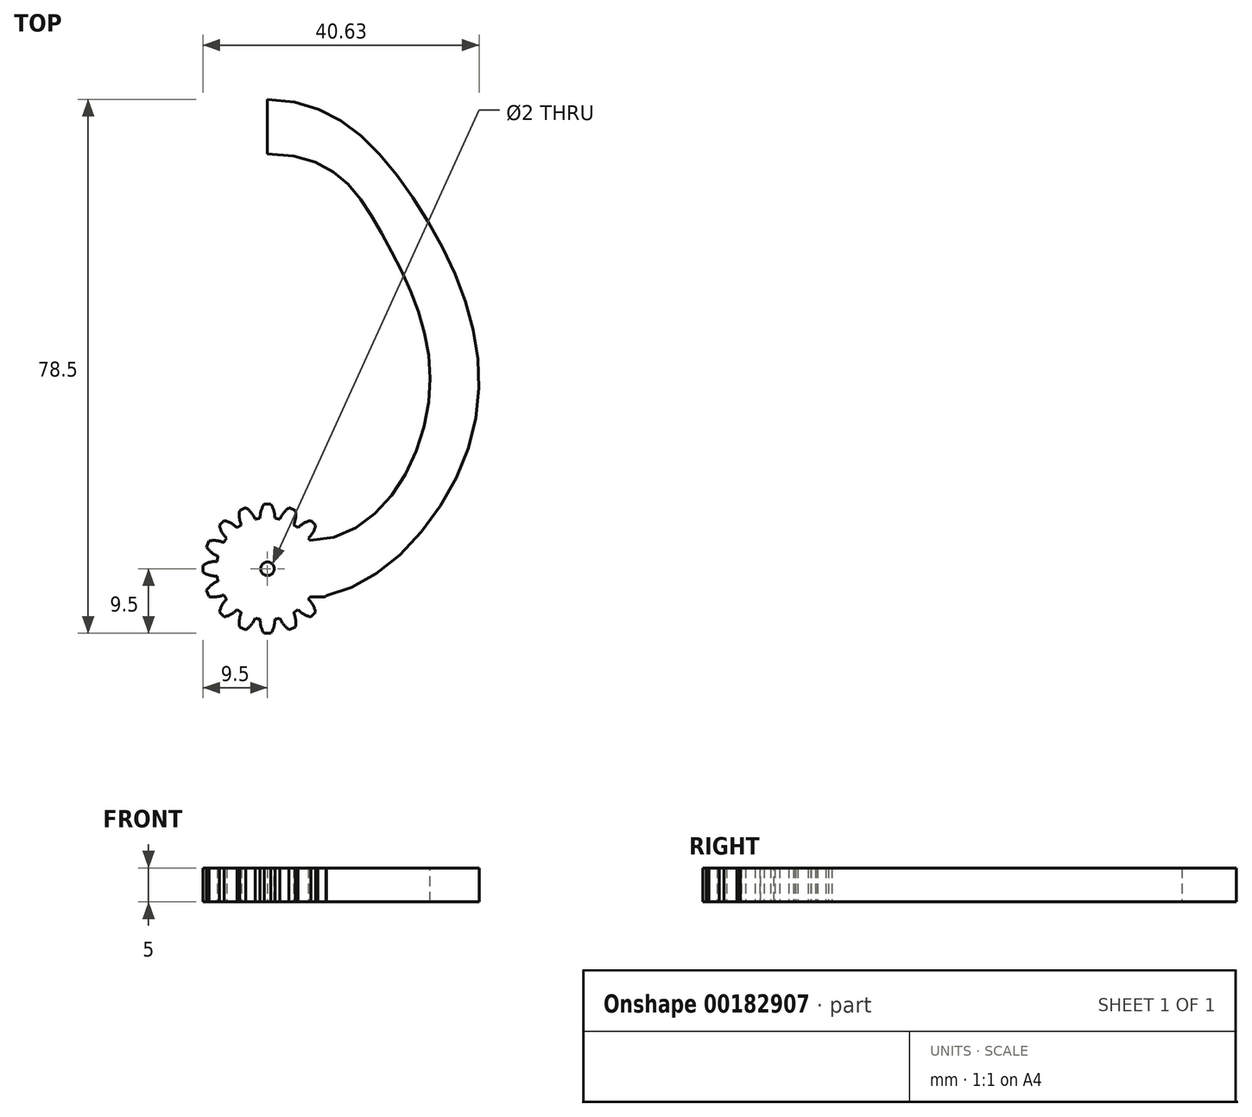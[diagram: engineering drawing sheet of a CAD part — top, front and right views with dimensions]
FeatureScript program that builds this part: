
annotation { "Feature Type Name" : "Feature", "Feature Type Description" : "" }
export const myFeature = defineFeature(function(context is Context, id is Id, definition is map)
    precondition{}
    {
        {
            var Q0;
            Q0=qCreatedBy(makeId("Top.planeOp"),FACE);
            var sketch = newSketch(context, id + "F0", { "sketchPlane" : qUnion([Q0])});
            skCircle(sketch, "E0", {"center": v(0, 0) * mm, "radius": 7.5 * mm});
            skLineSegment(sketch, "E1", {"start": v(0, 0) * mm, "end": v(0, 7.5) * mm, "construction": true});
            skLineSegment(sketch, "E2", {"start": v(0, 7.5) * mm, "end": v(0, 9.5) * mm, "construction": true});
            skLineSegment(sketch, "E3", {"start": v(0, 9.5) * mm, "end": v(-0.5, 9.5) * mm});
            skArc(sketch, "E4", {"start": v(-0.5, 9.5) * mm, "mid": v(-0.95, 8.5) * mm, "end": v(-1.09, 7.42) * mm});
            skLineSegment(sketch, "E5.MirrorCS", {"start": v(0, 9.5) * mm, "end": v(0.5, 9.5) * mm});
            skArc(sketch, "E6.MirrorCS", {"start": v(0.5, 9.5) * mm, "mid": v(0.95, 8.5) * mm, "end": v(1.09, 7.42) * mm});
            skArc(sketch, "E7.1.0", {"start": v(-4.1, 8.59) * mm, "mid": v(-4.13, 7.5) * mm, "end": v(-3.85, 6.44) * mm});
            skLineSegment(sketch, "E7.1.1", {"start": v(-3.64, 8.78) * mm, "end": v(-4.1, 8.59) * mm});
            skLineSegment(sketch, "E7.1.2", {"start": v(-3.64, 8.78) * mm, "end": v(-3.17, 8.97) * mm});
            skArc(sketch, "E7.1.3", {"start": v(-3.17, 8.97) * mm, "mid": v(-2.38, 8.22) * mm, "end": v(-1.83, 7.27) * mm});
            skArc(sketch, "E7.2.0", {"start": v(-7.07, 6.36) * mm, "mid": v(-6.69, 5.34) * mm, "end": v(-6.02, 4.48) * mm});
            skLineSegment(sketch, "E7.2.1", {"start": v(-6.72, 6.72) * mm, "end": v(-7.07, 6.36) * mm});
            skLineSegment(sketch, "E7.2.2", {"start": v(-6.72, 6.72) * mm, "end": v(-6.36, 7.07) * mm});
            skArc(sketch, "E7.2.3", {"start": v(-6.36, 7.07) * mm, "mid": v(-5.34, 6.69) * mm, "end": v(-4.48, 6.02) * mm});
            skArc(sketch, "E7.3.0", {"start": v(-8.97, 3.17) * mm, "mid": v(-8.22, 2.38) * mm, "end": v(-7.27, 1.83) * mm});
            skLineSegment(sketch, "E7.3.1", {"start": v(-8.78, 3.64) * mm, "end": v(-8.97, 3.17) * mm});
            skLineSegment(sketch, "E7.3.2", {"start": v(-8.78, 3.64) * mm, "end": v(-8.59, 4.1) * mm});
            skArc(sketch, "E7.3.3", {"start": v(-8.59, 4.1) * mm, "mid": v(-7.5, 4.13) * mm, "end": v(-6.44, 3.85) * mm});
            skArc(sketch, "E7.4.0", {"start": v(-9.5, -0.5) * mm, "mid": v(-8.5, -0.95) * mm, "end": v(-7.42, -1.09) * mm});
            skLineSegment(sketch, "E7.4.1", {"start": v(-9.5, 0) * mm, "end": v(-9.5, -0.5) * mm});
            skLineSegment(sketch, "E7.4.2", {"start": v(-9.5, 0) * mm, "end": v(-9.5, 0.5) * mm});
            skArc(sketch, "E7.4.3", {"start": v(-9.5, 0.5) * mm, "mid": v(-8.5, 0.95) * mm, "end": v(-7.42, 1.09) * mm});
            skArc(sketch, "E7.5.0", {"start": v(-8.59, -4.1) * mm, "mid": v(-7.5, -4.13) * mm, "end": v(-6.44, -3.85) * mm});
            skLineSegment(sketch, "E7.5.1", {"start": v(-8.78, -3.64) * mm, "end": v(-8.59, -4.1) * mm});
            skLineSegment(sketch, "E7.5.2", {"start": v(-8.78, -3.64) * mm, "end": v(-8.97, -3.17) * mm});
            skArc(sketch, "E7.5.3", {"start": v(-8.97, -3.17) * mm, "mid": v(-8.22, -2.38) * mm, "end": v(-7.27, -1.83) * mm});
            skArc(sketch, "E7.6.0", {"start": v(-6.36, -7.07) * mm, "mid": v(-5.34, -6.69) * mm, "end": v(-4.48, -6.02) * mm});
            skLineSegment(sketch, "E7.6.1", {"start": v(-6.72, -6.72) * mm, "end": v(-6.36, -7.07) * mm});
            skLineSegment(sketch, "E7.6.2", {"start": v(-6.72, -6.72) * mm, "end": v(-7.07, -6.36) * mm});
            skArc(sketch, "E7.6.3", {"start": v(-7.07, -6.36) * mm, "mid": v(-6.69, -5.34) * mm, "end": v(-6.02, -4.48) * mm});
            skArc(sketch, "E7.7.0", {"start": v(-3.17, -8.97) * mm, "mid": v(-2.38, -8.22) * mm, "end": v(-1.83, -7.27) * mm});
            skLineSegment(sketch, "E7.7.1", {"start": v(-3.64, -8.78) * mm, "end": v(-3.17, -8.97) * mm});
            skLineSegment(sketch, "E7.7.2", {"start": v(-3.64, -8.78) * mm, "end": v(-4.1, -8.59) * mm});
            skArc(sketch, "E7.7.3", {"start": v(-4.1, -8.59) * mm, "mid": v(-4.13, -7.5) * mm, "end": v(-3.85, -6.44) * mm});
            skArc(sketch, "E7.8.0", {"start": v(0.5, -9.5) * mm, "mid": v(0.95, -8.5) * mm, "end": v(1.09, -7.42) * mm});
            skLineSegment(sketch, "E7.8.1", {"start": v(0, -9.5) * mm, "end": v(0.5, -9.5) * mm});
            skLineSegment(sketch, "E7.8.2", {"start": v(0, -9.5) * mm, "end": v(-0.5, -9.5) * mm});
            skArc(sketch, "E7.8.3", {"start": v(-0.5, -9.5) * mm, "mid": v(-0.95, -8.5) * mm, "end": v(-1.09, -7.42) * mm});
            skArc(sketch, "E7.9.0", {"start": v(4.1, -8.59) * mm, "mid": v(4.13, -7.5) * mm, "end": v(3.85, -6.44) * mm});
            skLineSegment(sketch, "E7.9.1", {"start": v(3.64, -8.78) * mm, "end": v(4.1, -8.59) * mm});
            skLineSegment(sketch, "E7.9.2", {"start": v(3.64, -8.78) * mm, "end": v(3.17, -8.97) * mm});
            skArc(sketch, "E7.9.3", {"start": v(3.17, -8.97) * mm, "mid": v(2.38, -8.22) * mm, "end": v(1.83, -7.27) * mm});
            skArc(sketch, "E7.10.0", {"start": v(7.07, -6.36) * mm, "mid": v(6.69, -5.34) * mm, "end": v(6.02, -4.48) * mm});
            skLineSegment(sketch, "E7.10.1", {"start": v(6.72, -6.72) * mm, "end": v(7.07, -6.36) * mm});
            skLineSegment(sketch, "E7.10.2", {"start": v(6.72, -6.72) * mm, "end": v(6.36, -7.07) * mm});
            skArc(sketch, "E7.10.3", {"start": v(6.36, -7.07) * mm, "mid": v(5.34, -6.69) * mm, "end": v(4.48, -6.02) * mm});
            skArc(sketch, "E7.11.0", {"start": v(8.97, -3.17) * mm, "mid": v(8.22, -2.38) * mm, "end": v(7.27, -1.83) * mm});
            skLineSegment(sketch, "E7.11.1", {"start": v(8.78, -3.64) * mm, "end": v(8.97, -3.17) * mm});
            skLineSegment(sketch, "E7.11.2", {"start": v(8.78, -3.64) * mm, "end": v(8.59, -4.1) * mm});
            skArc(sketch, "E7.11.3", {"start": v(8.59, -4.1) * mm, "mid": v(7.5, -4.13) * mm, "end": v(6.44, -3.85) * mm});
            skArc(sketch, "E7.12.0", {"start": v(9.5, 0.5) * mm, "mid": v(8.5, 0.95) * mm, "end": v(7.42, 1.09) * mm});
            skLineSegment(sketch, "E7.12.1", {"start": v(9.5, 0) * mm, "end": v(9.5, 0.5) * mm});
            skLineSegment(sketch, "E7.12.2", {"start": v(9.5, 0) * mm, "end": v(9.5, -0.5) * mm});
            skArc(sketch, "E7.12.3", {"start": v(9.5, -0.5) * mm, "mid": v(8.5, -0.95) * mm, "end": v(7.42, -1.09) * mm});
            skArc(sketch, "E7.13.0", {"start": v(8.59, 4.1) * mm, "mid": v(7.5, 4.13) * mm, "end": v(6.44, 3.85) * mm});
            skLineSegment(sketch, "E7.13.1", {"start": v(8.78, 3.64) * mm, "end": v(8.59, 4.1) * mm});
            skLineSegment(sketch, "E7.13.2", {"start": v(8.78, 3.64) * mm, "end": v(8.97, 3.17) * mm});
            skArc(sketch, "E7.13.3", {"start": v(8.97, 3.17) * mm, "mid": v(8.22, 2.38) * mm, "end": v(7.27, 1.83) * mm});
            skArc(sketch, "E7.14.0", {"start": v(6.36, 7.07) * mm, "mid": v(5.34, 6.69) * mm, "end": v(4.48, 6.02) * mm});
            skLineSegment(sketch, "E7.14.1", {"start": v(6.72, 6.72) * mm, "end": v(6.36, 7.07) * mm});
            skLineSegment(sketch, "E7.14.2", {"start": v(6.72, 6.72) * mm, "end": v(7.07, 6.36) * mm});
            skArc(sketch, "E7.14.3", {"start": v(7.07, 6.36) * mm, "mid": v(6.69, 5.34) * mm, "end": v(6.02, 4.48) * mm});
            skArc(sketch, "E7.15.0", {"start": v(3.17, 8.97) * mm, "mid": v(2.38, 8.22) * mm, "end": v(1.83, 7.27) * mm});
            skLineSegment(sketch, "E7.15.1", {"start": v(3.64, 8.78) * mm, "end": v(3.17, 8.97) * mm});
            skLineSegment(sketch, "E7.15.2", {"start": v(3.64, 8.78) * mm, "end": v(4.1, 8.59) * mm});
            skArc(sketch, "E7.15.3", {"start": v(4.1, 8.59) * mm, "mid": v(4.13, 7.5) * mm, "end": v(3.85, 6.44) * mm});
            skSolve(sketch);
        }
        {
            var Q0;
            Q0=qSketchRegion(id+"F0",true);
            extrude(context, id + "F1", {"entities" : qUnion([Q0]), "depth" : 5 * mm});
        }
        {
            var Q0;
            Q0=makeQuery(id+"F1.opExtrude","CAP_FACE",FACE,{"disambiguationData":[OSD([sQuery(id+"F0.wireOp",EDGE,"E0"),sQuery(id+"F0.wireOp",EDGE,"E3"),sQuery(id+"F0.wireOp",EDGE,"E4"),sQuery(id+"F0.wireOp",EDGE,"E5.MirrorCS"),sQuery(id+"F0.wireOp",EDGE,"E6.MirrorCS"),sQuery(id+"F0.wireOp",EDGE,"E7.1.0"),sQuery(id+"F0.wireOp",EDGE,"E7.1.1"),sQuery(id+"F0.wireOp",EDGE,"E7.1.2"),sQuery(id+"F0.wireOp",EDGE,"E7.1.3"),sQuery(id+"F0.wireOp",EDGE,"E7.2.0"),sQuery(id+"F0.wireOp",EDGE,"E7.2.1"),sQuery(id+"F0.wireOp",EDGE,"E7.2.2"),sQuery(id+"F0.wireOp",EDGE,"E7.2.3"),sQuery(id+"F0.wireOp",EDGE,"E7.3.0"),sQuery(id+"F0.wireOp",EDGE,"E7.3.1"),sQuery(id+"F0.wireOp",EDGE,"E7.3.2"),sQuery(id+"F0.wireOp",EDGE,"E7.3.3"),sQuery(id+"F0.wireOp",EDGE,"E7.4.0"),sQuery(id+"F0.wireOp",EDGE,"E7.4.1"),sQuery(id+"F0.wireOp",EDGE,"E7.4.2"),sQuery(id+"F0.wireOp",EDGE,"E7.4.3"),sQuery(id+"F0.wireOp",EDGE,"E7.5.0"),sQuery(id+"F0.wireOp",EDGE,"E7.5.1"),sQuery(id+"F0.wireOp",EDGE,"E7.5.2"),sQuery(id+"F0.wireOp",EDGE,"E7.5.3"),sQuery(id+"F0.wireOp",EDGE,"E7.6.0"),sQuery(id+"F0.wireOp",EDGE,"E7.6.1"),sQuery(id+"F0.wireOp",EDGE,"E7.6.2"),sQuery(id+"F0.wireOp",EDGE,"E7.6.3"),sQuery(id+"F0.wireOp",EDGE,"E7.7.0"),sQuery(id+"F0.wireOp",EDGE,"E7.7.1"),sQuery(id+"F0.wireOp",EDGE,"E7.7.2"),sQuery(id+"F0.wireOp",EDGE,"E7.7.3"),sQuery(id+"F0.wireOp",EDGE,"E7.8.0"),sQuery(id+"F0.wireOp",EDGE,"E7.8.1"),sQuery(id+"F0.wireOp",EDGE,"E7.8.2"),sQuery(id+"F0.wireOp",EDGE,"E7.8.3"),sQuery(id+"F0.wireOp",EDGE,"E7.9.0"),sQuery(id+"F0.wireOp",EDGE,"E7.9.1"),sQuery(id+"F0.wireOp",EDGE,"E7.9.2"),sQuery(id+"F0.wireOp",EDGE,"E7.9.3"),sQuery(id+"F0.wireOp",EDGE,"E7.10.0"),sQuery(id+"F0.wireOp",EDGE,"E7.10.1"),sQuery(id+"F0.wireOp",EDGE,"E7.10.2"),sQuery(id+"F0.wireOp",EDGE,"E7.10.3"),sQuery(id+"F0.wireOp",EDGE,"E7.11.0"),sQuery(id+"F0.wireOp",EDGE,"E7.11.1"),sQuery(id+"F0.wireOp",EDGE,"E7.11.2"),sQuery(id+"F0.wireOp",EDGE,"E7.11.3"),sQuery(id+"F0.wireOp",EDGE,"E7.12.0"),sQuery(id+"F0.wireOp",EDGE,"E7.12.1"),sQuery(id+"F0.wireOp",EDGE,"E7.12.2"),sQuery(id+"F0.wireOp",EDGE,"E7.12.3"),sQuery(id+"F0.wireOp",EDGE,"E7.13.0"),sQuery(id+"F0.wireOp",EDGE,"E7.13.1"),sQuery(id+"F0.wireOp",EDGE,"E7.13.2"),sQuery(id+"F0.wireOp",EDGE,"E7.13.3"),sQuery(id+"F0.wireOp",EDGE,"E7.14.0"),sQuery(id+"F0.wireOp",EDGE,"E7.14.1"),sQuery(id+"F0.wireOp",EDGE,"E7.14.2"),sQuery(id+"F0.wireOp",EDGE,"E7.14.3"),sQuery(id+"F0.wireOp",EDGE,"E7.15.0"),sQuery(id+"F0.wireOp",EDGE,"E7.15.1"),sQuery(id+"F0.wireOp",EDGE,"E7.15.2"),sQuery(id+"F0.wireOp",EDGE,"E7.15.3")])],"isStart":false});
            var sketch = newSketch(context, id + "F2", { "sketchPlane" : qUnion([Q0])});
            skCircle(sketch, "E8", {"center": v(0, 0) * mm, "radius": 1 * mm});
            skSolve(sketch);
        }
        {
            var Q0;
            Q0=qSketchRegion(id+"F2",true);
            extrude(context, id + "F3", {"entities" : qUnion([Q0]), "operationType" : NewBodyOperationType.REMOVE, "endBound" : BoundingType.THROUGH_ALL, "oppositeDirection" : true, "depth" : 25 * mm});
        }
        {
            var Q0;
            Q0=qCreatedBy(makeId("Top.planeOp"),FACE);
            var sketch = newSketch(context, id + "F4", { "sketchPlane" : qUnion([Q0])});
            skLineSegment(sketch, "E9", {"start": v(0, 69) * mm, "end": v(0, 61) * mm});
            skFitSpline(sketch, "E10", {"points": [v(0, 61) * mm, v(16.92, 49.1) * mm, v(23.78, 24.9) * mm, v(6.24, 4.17) * mm], "startDerivative": vector(97.47, 0) * mm, "endDerivative": vector(-85.06, 0) * mm});
            skFitSpline(sketch, "E11", {"points": [v(0, 69) * mm, v(21.94, 53.74) * mm, v(30.22, 20.02) * mm, v(6.24, -4.17) * mm], "startDerivative": vector(98.06, 0) * mm, "endDerivative": vector(-86.86, 0) * mm});
            skLineSegment(sketch, "E12", {"start": v(6.24, 4.17) * mm, "end": v(6.24, -4.17) * mm});
            skSolve(sketch);
        }
        {
            var Q0;
            Q0 = qSketchRegion(id + "F4", true);
            var Q1;
            Q1=makeQuery(id+"F1.opExtrude","CAP_FACE",FACE,{"disambiguationData":[OSD([sQuery(id+"F0.wireOp",EDGE,"E0"),sQuery(id+"F0.wireOp",EDGE,"E3"),sQuery(id+"F0.wireOp",EDGE,"E4"),sQuery(id+"F0.wireOp",EDGE,"E5.MirrorCS"),sQuery(id+"F0.wireOp",EDGE,"E6.MirrorCS"),sQuery(id+"F0.wireOp",EDGE,"E7.1.0"),sQuery(id+"F0.wireOp",EDGE,"E7.1.1"),sQuery(id+"F0.wireOp",EDGE,"E7.1.2"),sQuery(id+"F0.wireOp",EDGE,"E7.1.3"),sQuery(id+"F0.wireOp",EDGE,"E7.2.0"),sQuery(id+"F0.wireOp",EDGE,"E7.2.1"),sQuery(id+"F0.wireOp",EDGE,"E7.2.2"),sQuery(id+"F0.wireOp",EDGE,"E7.2.3"),sQuery(id+"F0.wireOp",EDGE,"E7.3.0"),sQuery(id+"F0.wireOp",EDGE,"E7.3.1"),sQuery(id+"F0.wireOp",EDGE,"E7.3.2"),sQuery(id+"F0.wireOp",EDGE,"E7.3.3"),sQuery(id+"F0.wireOp",EDGE,"E7.4.0"),sQuery(id+"F0.wireOp",EDGE,"E7.4.1"),sQuery(id+"F0.wireOp",EDGE,"E7.4.2"),sQuery(id+"F0.wireOp",EDGE,"E7.4.3"),sQuery(id+"F0.wireOp",EDGE,"E7.5.0"),sQuery(id+"F0.wireOp",EDGE,"E7.5.1"),sQuery(id+"F0.wireOp",EDGE,"E7.5.2"),sQuery(id+"F0.wireOp",EDGE,"E7.5.3"),sQuery(id+"F0.wireOp",EDGE,"E7.6.0"),sQuery(id+"F0.wireOp",EDGE,"E7.6.1"),sQuery(id+"F0.wireOp",EDGE,"E7.6.2"),sQuery(id+"F0.wireOp",EDGE,"E7.6.3"),sQuery(id+"F0.wireOp",EDGE,"E7.7.0"),sQuery(id+"F0.wireOp",EDGE,"E7.7.1"),sQuery(id+"F0.wireOp",EDGE,"E7.7.2"),sQuery(id+"F0.wireOp",EDGE,"E7.7.3"),sQuery(id+"F0.wireOp",EDGE,"E7.8.0"),sQuery(id+"F0.wireOp",EDGE,"E7.8.1"),sQuery(id+"F0.wireOp",EDGE,"E7.8.2"),sQuery(id+"F0.wireOp",EDGE,"E7.8.3"),sQuery(id+"F0.wireOp",EDGE,"E7.9.0"),sQuery(id+"F0.wireOp",EDGE,"E7.9.1"),sQuery(id+"F0.wireOp",EDGE,"E7.9.2"),sQuery(id+"F0.wireOp",EDGE,"E7.9.3"),sQuery(id+"F0.wireOp",EDGE,"E7.10.0"),sQuery(id+"F0.wireOp",EDGE,"E7.10.1"),sQuery(id+"F0.wireOp",EDGE,"E7.10.2"),sQuery(id+"F0.wireOp",EDGE,"E7.10.3"),sQuery(id+"F0.wireOp",EDGE,"E7.11.0"),sQuery(id+"F0.wireOp",EDGE,"E7.11.1"),sQuery(id+"F0.wireOp",EDGE,"E7.11.2"),sQuery(id+"F0.wireOp",EDGE,"E7.11.3"),sQuery(id+"F0.wireOp",EDGE,"E7.12.0"),sQuery(id+"F0.wireOp",EDGE,"E7.12.1"),sQuery(id+"F0.wireOp",EDGE,"E7.12.2"),sQuery(id+"F0.wireOp",EDGE,"E7.12.3"),sQuery(id+"F0.wireOp",EDGE,"E7.13.0"),sQuery(id+"F0.wireOp",EDGE,"E7.13.1"),sQuery(id+"F0.wireOp",EDGE,"E7.13.2"),sQuery(id+"F0.wireOp",EDGE,"E7.13.3"),sQuery(id+"F0.wireOp",EDGE,"E7.14.0"),sQuery(id+"F0.wireOp",EDGE,"E7.14.1"),sQuery(id+"F0.wireOp",EDGE,"E7.14.2"),sQuery(id+"F0.wireOp",EDGE,"E7.14.3"),sQuery(id+"F0.wireOp",EDGE,"E7.15.0"),sQuery(id+"F0.wireOp",EDGE,"E7.15.1"),sQuery(id+"F0.wireOp",EDGE,"E7.15.2"),sQuery(id+"F0.wireOp",EDGE,"E7.15.3")])],"isStart":false});
            extrude(context, id + "F5", {"entities" : qUnion([Q0]), "operationType" : NewBodyOperationType.ADD, "endBound" : BoundingType.UP_TO_SURFACE, "endBoundEntityFace" : qUnion([Q1]), "depth" : 25 * mm});
        }
    });
